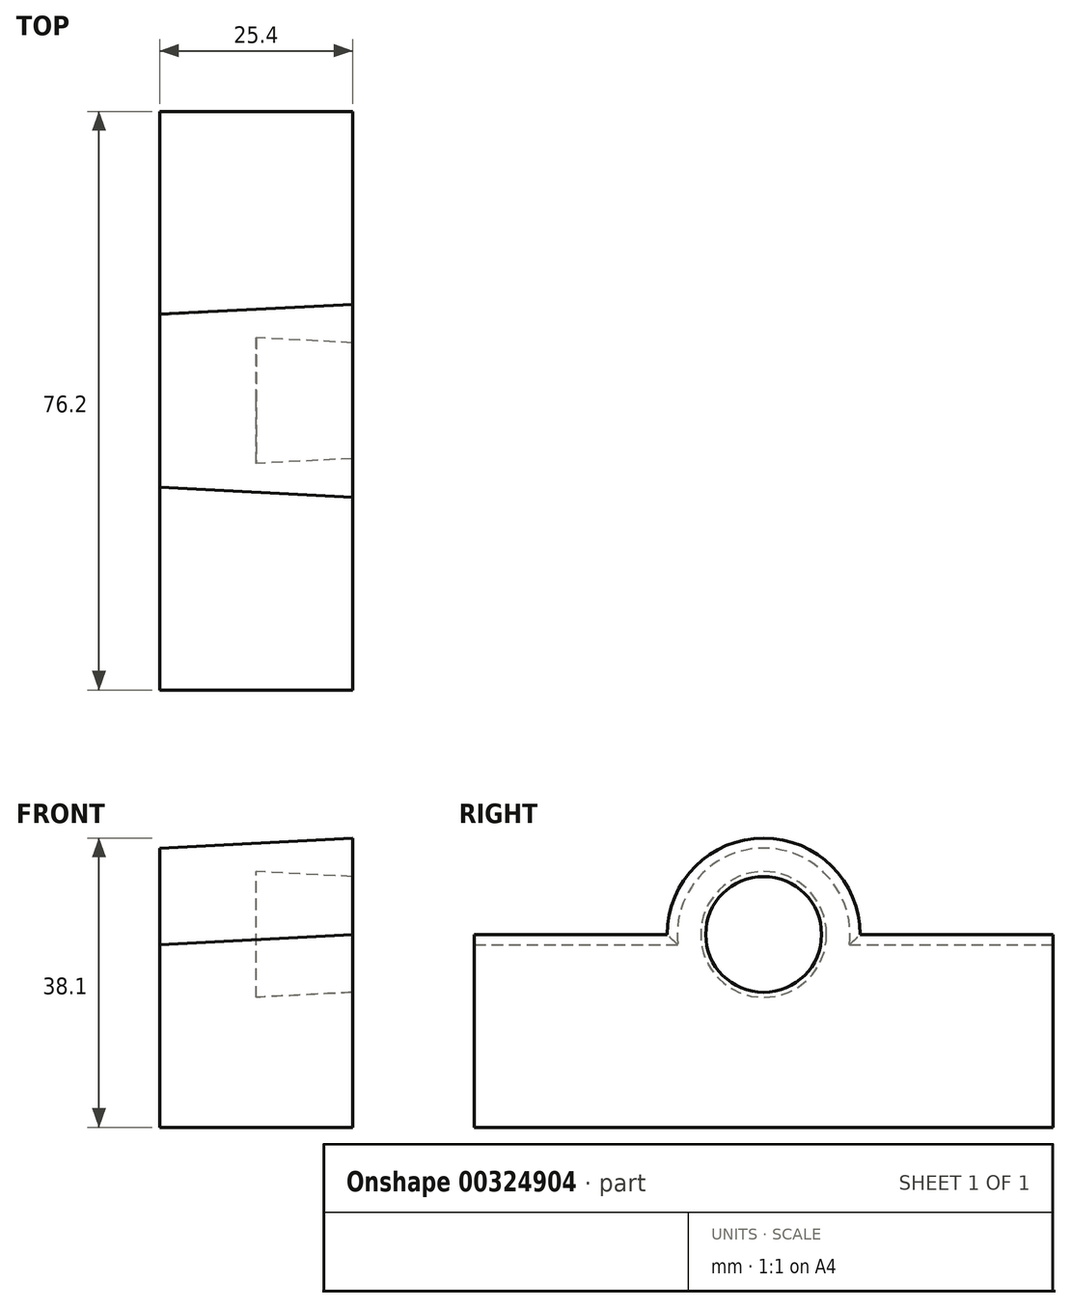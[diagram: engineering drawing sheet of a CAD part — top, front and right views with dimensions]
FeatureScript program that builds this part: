
annotation { "Feature Type Name" : "Feature", "Feature Type Description" : "" }
export const myFeature = defineFeature(function(context is Context, id is Id, definition is map)
    precondition{}
    {
        {
            var Q0;
            Q0=qCreatedBy(makeId("Right.planeOp"),FACE);
            var sketch = newSketch(context, id + "F0", { "sketchPlane" : qUnion([Q0])});
            skLineSegment(sketch, "E0", {"start": v(0, 17.15) * mm, "end": v(-76.2, 17.15) * mm});
            skLineSegment(sketch, "E1", {"start": v(-76.2, 17.15) * mm, "end": v(-76.2, 67.95) * mm});
            skLineSegment(sketch, "E2", {"start": v(-76.2, 67.95) * mm, "end": v(0, 67.95) * mm});
            skLineSegment(sketch, "E3", {"start": v(0, 67.95) * mm, "end": v(0, 17.15) * mm});
            skSolve(sketch);
        }
        {
            var Q0;
            Q0=makeQuery(id+"F0.imprint","IMPRINT",FACE,{"disambiguationData":[TD([[makeQuery(id+"F0.imprint","IMPRINT",EDGE,{"derivedFrom":sQuery(id+"F0.wireOp",EDGE,"E0")}),-1.0]])]});
            extrude(context, id + "F1", {"entities" : qUnion([Q0]), "depth" : 25.4 * mm});
        }
        {
            var Q0;
            Q0=makeQuery(id+"F1.opExtrude","CAP_FACE",FACE,{"disambiguationData":[OSD([sQuery(id+"F0.wireOp",EDGE,"E0"),sQuery(id+"F0.wireOp",EDGE,"E1"),sQuery(id+"F0.wireOp",EDGE,"E2"),sQuery(id+"F0.wireOp",EDGE,"E3")])],"isStart":false});
            var sketch = newSketch(context, id + "F2", { "sketchPlane" : qUnion([Q0])});
            skCircle(sketch, "E4", {"center": v(-38.1, 42.55) * mm, "radius": 12.7 * mm});
            skPoint(sketch, "E4.centerSnap0", {"position": v(-76.2, 42.55) * mm});
            skPoint(sketch, "E4.centerSnap1", {"position": v(-38.1, 67.95) * mm});
            skLineSegment(sketch, "E5", {"start": v(-76.2, 42.55) * mm, "end": v(-50.8, 42.55) * mm});
            skLineSegment(sketch, "E6", {"start": v(-25.4, 42.55) * mm, "end": v(0, 42.55) * mm});
            skPoint(sketch, "E6.endSnap0", {"position": v(0, 42.55) * mm});
            skLineSegment(sketch, "E7", {"start": v(-76.2, 42.55) * mm, "end": v(-76.2, 67.95) * mm});
            skLineSegment(sketch, "E8", {"start": v(-76.2, 67.95) * mm, "end": v(0, 67.95) * mm});
            skLineSegment(sketch, "E9", {"start": v(0, 67.95) * mm, "end": v(0, 42.55) * mm});
            skSolve(sketch);
        }
        {
            var Q0;
            {var subQ1=sQuery(id+"F2.wireOp",EDGE,"E5");Q0=makeQuery(id+"F2.imprint","IMPRINT",FACE,{"disambiguationData":[TD([[makeQuery(id+"F2.imprint","IMPRINT",EDGE,{"derivedFrom":subQ1}),1.0]])]});}
            extrude(context, id + "F3", {"entities" : qUnion([Q0]), "operationType" : NewBodyOperationType.REMOVE, "oppositeDirection" : true, "depth" : 25.4 * mm, "hasDraft" : true, "draftAngle" : 3 * degree});
        }
        {
            var Q0;
            Q0=makeQuery(id+"F1.opExtrude","CAP_FACE",FACE,{"disambiguationData":[OSD([sQuery(id+"F0.wireOp",EDGE,"E0"),sQuery(id+"F0.wireOp",EDGE,"E1"),sQuery(id+"F0.wireOp",EDGE,"E2"),sQuery(id+"F0.wireOp",EDGE,"E3")])],"isStart":false});
            var sketch = newSketch(context, id + "F4", { "sketchPlane" : qUnion([Q0])});
            skCircle(sketch, "E10", {"center": v(-38.1, 42.55) * mm, "radius": 7.62 * mm});
            skSolve(sketch);
        }
        {
            var Q0;
            Q0 = qSketchRegion(id + "F4", true);
            extrude(context, id + "F5", {"entities" : qUnion([Q0]), "operationType" : NewBodyOperationType.REMOVE, "oppositeDirection" : true, "depth" : 12.7 * mm, "hasDraft" : true, "draftAngle" : 3 * degree});
        }
    });
